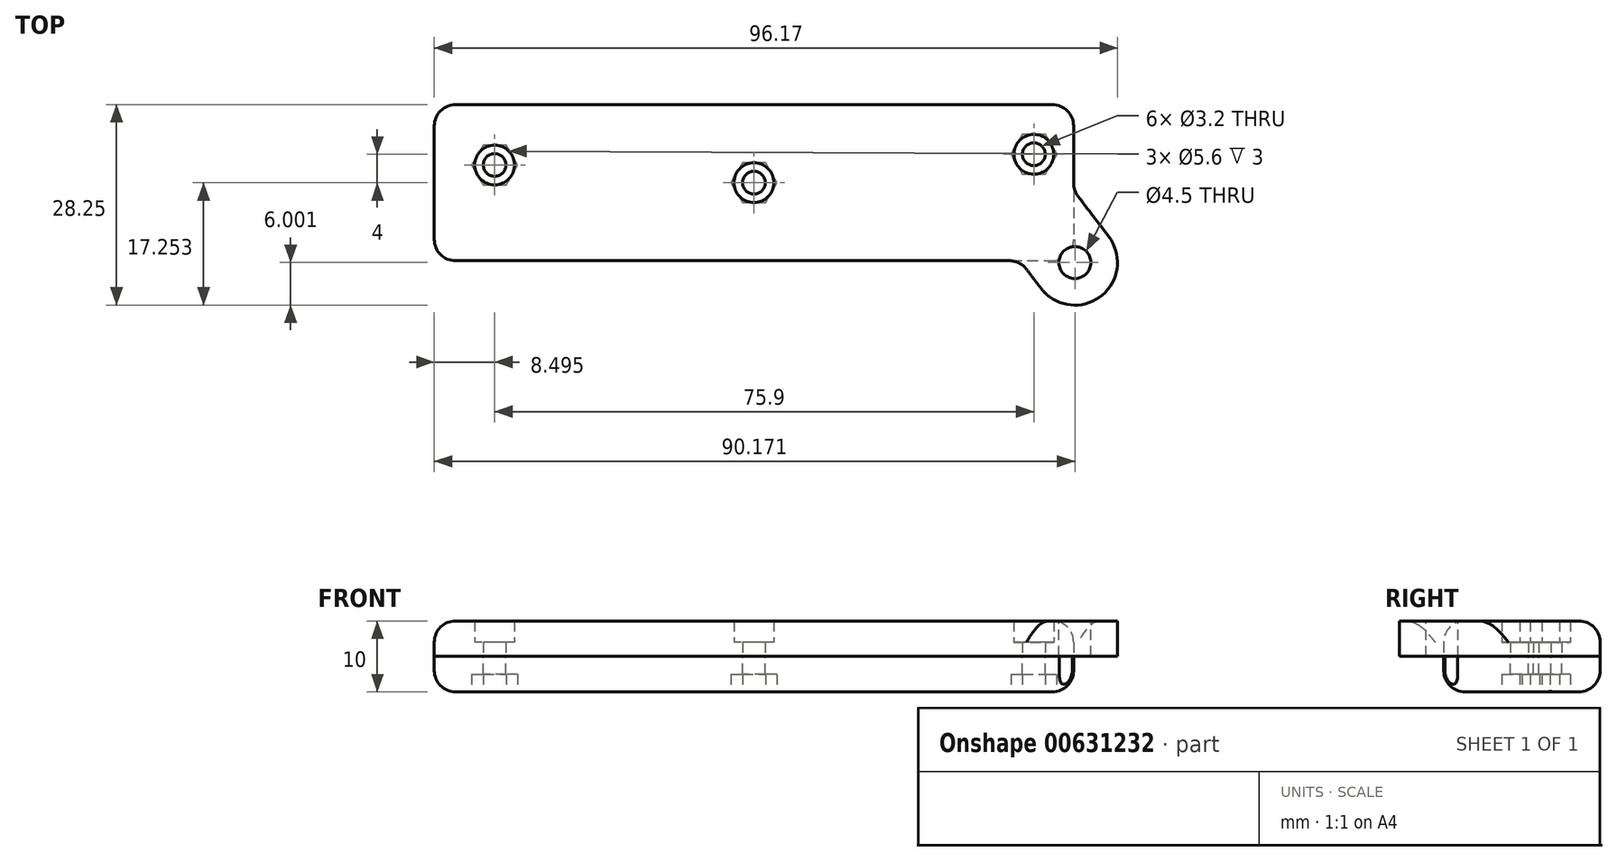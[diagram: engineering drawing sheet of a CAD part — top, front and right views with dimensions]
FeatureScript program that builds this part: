
annotation { "Feature Type Name" : "Feature", "Feature Type Description" : "" }
export const myFeature = defineFeature(function(context is Context, id is Id, definition is map)
    precondition{}
    {
        {
            var Q0;
            Q0=qCreatedBy(makeId("Top.planeOp"),FACE);
            var sketch = newSketch(context, id + "F0", { "sketchPlane" : qUnion([Q0])});
            skLineSegment(sketch, "E0.bottom", {"start": v(-43.13, 4.52) * mm, "end": v(46.87, 4.52) * mm});
            skLineSegment(sketch, "E0.top", {"start": v(-43.13, -17.48) * mm, "end": v(46.87, -17.48) * mm});
            skLineSegment(sketch, "E0.left", {"start": v(-43.13, 4.52) * mm, "end": v(-43.13, -17.48) * mm});
            skLineSegment(sketch, "E0.right", {"start": v(46.87, 4.52) * mm, "end": v(46.87, -17.48) * mm});
            skCircle(sketch, "E1", {"center": v(-34.63, -3.98) * mm, "radius": 1.6 * mm});
            skCircle(sketch, "E2", {"center": v(41.27, -2.48) * mm, "radius": 1.6 * mm});
            skCircle(sketch, "E3", {"center": v(1.87, -6.48) * mm, "radius": 1.6 * mm});
            skCircle(sketch, "E4", {"center": v(47.04, -17.73) * mm, "radius": 6 * mm});
            skLineSegment(sketch, "E5", {"start": v(42.26, -21.35) * mm, "end": v(39.32, -17.48) * mm});
            skLineSegment(sketch, "E6", {"start": v(42.26, -21.35) * mm, "end": v(51.82, -14.1) * mm, "construction": true});
            skLineSegment(sketch, "E7", {"start": v(51.82, -14.1) * mm, "end": v(46.87, -7.56) * mm});
            skSolve(sketch);
        }
        {
            var Q0;
            Q0=makeQuery(id+"F0.imprint","IMPRINT",FACE,{"disambiguationData":[TD([[makeQuery(id+"F0.imprint","IMPRINT",EDGE,{"derivedFrom":sQuery(id+"F0.wireOp",EDGE,"E0.bottom")}),-1.0]])]});
            var Q1;
            {var subQ0=sQuery(id+"F0.wireOp",EDGE,"E5");Q1=makeQuery(id+"F0.imprint","IMPRINT",FACE,{"disambiguationData":[TD([[makeQuery(id+"F0.imprint","IMPRINT",EDGE,{"derivedFrom":subQ0}),-1.0]])]});}
            var Q2;
            {var subQ0=sQuery(id+"F0.wireOp",EDGE,"E0.right");var subQ1=sQuery(id+"F0.wireOp",EDGE,"E0.top");var subQ2=makeQuery(id+"F0.imprint","INTERSECT",VERTEX,{"derivedFrom":[subQ1,subQ0]});Q2=makeQuery(id+"F0.imprint","IMPRINT",FACE,{"disambiguationData":[TD([[makeQuery(id+"F0.imprint","IMPRINT",EDGE,{"disambiguationData":[TD([[subQ2,1.0]])],"derivedFrom":subQ1}),1.0]])]});}
            var Q3;
            Q3=makeQuery(id+"F0.imprint","IMPRINT",FACE,{"disambiguationData":[TD([[makeQuery(id+"F0.imprint","IMPRINT",EDGE,{"derivedFrom":sQuery(id+"F0.wireOp",EDGE,"HLLScoW3-gvS7-jEic-zDn5-M5LXj1PQ8C7u")}),-1.0]])]});
            var Q4;
            {var subQ0=sQuery(id+"F0.wireOp",EDGE,"E7");Q4=makeQuery(id+"F0.imprint","IMPRINT",FACE,{"disambiguationData":[TD([[makeQuery(id+"F0.imprint","IMPRINT",EDGE,{"derivedFrom":subQ0}),1.0]])]});}
            var Q5;
            {var subQ2=sQuery(id+"F0.wireOp",EDGE,"E0.right");var subQ4=sQuery(id+"F0.wireOp",EDGE,"E0.top");var subQ5=makeQuery(id+"F0.imprint","INTERSECT",VERTEX,{"derivedFrom":[subQ4,subQ2]});Q5=makeQuery(id+"F0.imprint","IMPRINT",FACE,{"disambiguationData":[TD([[makeQuery(id+"F0.imprint","IMPRINT",EDGE,{"disambiguationData":[TD([[subQ5,1.0]])],"derivedFrom":subQ4}),-1.0]])]});}
            extrude(context, id + "F1", {"entities" : qUnion([Q0, Q1, Q2, Q3, Q4, Q5]), "depth" : 2 * mm, "offsetDistance" : 25 * mm});
        }
        {
            var Q0;
            Q0=makeQuery(id+"F1.opExtrude","CAP_FACE",FACE,{"disambiguationData":[OSD([sQuery(id+"F0.wireOp",EDGE,"E0.bottom"),sQuery(id+"F0.wireOp",EDGE,"E0.top"),sQuery(id+"F0.wireOp",EDGE,"E0.left"),sQuery(id+"F0.wireOp",EDGE,"E0.right"),sQuery(id+"F0.wireOp",EDGE,"E1"),sQuery(id+"F0.wireOp",EDGE,"E2"),sQuery(id+"F0.wireOp",EDGE,"E3")])],"isStart":false});
            var sketch = newSketch(context, id + "F2", { "sketchPlane" : qUnion([Q0])});
            skCircle(sketch, "E8.0", {"center": v(-34.63, -3.98) * mm, "radius": 2.8 * mm});
            skCircle(sketch, "E9.0", {"center": v(1.87, -6.48) * mm, "radius": 2.8 * mm});
            skCircle(sketch, "E10.0", {"center": v(41.27, -2.48) * mm, "radius": 2.8 * mm});
            skSolve(sketch);
        }
        {
            var Q0;
            Q0=makeQuery(id+"F2.imprint","IMPRINT",FACE,{"disambiguationData":[TD([[makeQuery(id+"F2.imprint","IMPRINT",EDGE,{"derivedFrom":sQuery(id+"F2.wireOp",EDGE,"E8.0")}),-1.0]])]});
            extrude(context, id + "F3", {"entities" : qUnion([Q0]), "operationType" : NewBodyOperationType.ADD, "depth" : 3 * mm, "offsetDistance" : 25 * mm});
        }
        {
            var Q0;
            Q0=makeQuery(id+"F3.opExtrude","CAP_EDGE",EDGE,{"disambiguationData":[OSD([sQuery(id+"F0.wireOp",EDGE,"E0.left")])],"isStart":false});
            var Q1;
            Q1=makeQuery(id+"F3.opExtrude","CAP_EDGE",EDGE,{"disambiguationData":[OSD([sQuery(id+"F0.wireOp",EDGE,"E0.bottom")])],"isStart":false});
            var Q2;
            Q2=makeQuery(id+"F3.opExtrude","CAP_EDGE",EDGE,{"disambiguationData":[OSD([sQuery(id+"F0.wireOp",EDGE,"E0.top")])],"isStart":false});
            var Q3;
            Q3=makeQuery(id+"F3.opExtrude","CAP_EDGE",EDGE,{"disambiguationData":[OSD([sQuery(id+"F0.wireOp",EDGE,"E0.right")])],"isStart":false});
            var Q4;
            {var subQ0=sQuery(id+"F0.wireOp",EDGE,"E0.right");var subQ1=sQuery(id+"F0.wireOp",EDGE,"E0.top");Q4=makeQuery(id+"F3.boolean.opBoolean","MERGE",EDGE,{"derivedFrom":[makeQuery(id+"F1.opExtrude","SWEPT_EDGE",EDGE,{"disambiguationData":[OSD([subQ1,subQ0])]}),makeQuery(id+"F3.opExtrude","SWEPT_EDGE",EDGE,{"disambiguationData":[OSD([subQ1,subQ0])]})]});}
            var Q5;
            {var subQ0=sQuery(id+"F0.wireOp",EDGE,"E0.right");var subQ1=sQuery(id+"F0.wireOp",EDGE,"E0.bottom");Q5=makeQuery(id+"F3.boolean.opBoolean","MERGE",EDGE,{"derivedFrom":[makeQuery(id+"F1.opExtrude","SWEPT_EDGE",EDGE,{"disambiguationData":[OSD([subQ1,subQ0])]}),makeQuery(id+"F3.opExtrude","SWEPT_EDGE",EDGE,{"disambiguationData":[OSD([subQ1,subQ0])]})]});}
            var Q6;
            {var subQ0=sQuery(id+"F0.wireOp",EDGE,"E0.left");var subQ1=sQuery(id+"F0.wireOp",EDGE,"E0.bottom");Q6=makeQuery(id+"F3.boolean.opBoolean","MERGE",EDGE,{"derivedFrom":[makeQuery(id+"F1.opExtrude","SWEPT_EDGE",EDGE,{"disambiguationData":[OSD([subQ1,subQ0])]}),makeQuery(id+"F3.opExtrude","SWEPT_EDGE",EDGE,{"disambiguationData":[OSD([subQ1,subQ0])]})]});}
            var Q7;
            {var subQ0=sQuery(id+"F0.wireOp",EDGE,"E0.left");var subQ1=sQuery(id+"F0.wireOp",EDGE,"E0.top");Q7=makeQuery(id+"F3.boolean.opBoolean","MERGE",EDGE,{"derivedFrom":[makeQuery(id+"F1.opExtrude","SWEPT_EDGE",EDGE,{"disambiguationData":[OSD([subQ1,subQ0])]}),makeQuery(id+"F3.opExtrude","SWEPT_EDGE",EDGE,{"disambiguationData":[OSD([subQ1,subQ0])]})]});}
            fillet(context, id + "F4", {"entities" : qUnion([Q0, Q1, Q2, Q3, Q4, Q5, Q6, Q7]), "radius" : 3 * mm, "tangentPropagation" : true, "allowEdgeOverflow" : false});
        }
        {
            var Q0;
            Q0=makeQuery(id+"F3.opExtrude","CAP_FACE",FACE,{"disambiguationData":[OSD([sQuery(id+"F0.wireOp",EDGE,"E0.bottom"),sQuery(id+"F0.wireOp",EDGE,"E0.top"),sQuery(id+"F0.wireOp",EDGE,"E0.left"),sQuery(id+"F0.wireOp",EDGE,"E0.right"),sQuery(id+"F0.wireOp",EDGE,"E4"),sQuery(id+"F0.wireOp",EDGE,"E5"),sQuery(id+"F0.wireOp",EDGE,"E7"),sQuery(id+"F2.wireOp",EDGE,"E8.0"),sQuery(id+"F2.wireOp",EDGE,"E9.0"),sQuery(id+"F2.wireOp",EDGE,"E10.0")])],"isStart":false});
            var sketch = newSketch(context, id + "F5", { "sketchPlane" : qUnion([Q0])});
            skCircle(sketch, "E11", {"center": v(47.04, -17.73) * mm, "radius": 2.25 * mm});
            skSolve(sketch);
        }
        {
            var Q0;
            Q0 = qSketchRegion(id + "F5", true);
            extrude(context, id + "F6", {"entities" : qUnion([Q0]), "operationType" : NewBodyOperationType.REMOVE, "endBound" : BoundingType.UP_TO_NEXT, "oppositeDirection" : true, "depth" : 25 * mm, "offsetDistance" : 25 * mm});
        }
        {
            var Q0;
            {var subQ7=sQuery(id+"F0.wireOp",EDGE,"E0.bottom");Q0=makeQuery(id+"F0.imprint","IMPRINT",FACE,{"disambiguationData":[TD([[makeQuery(id+"F0.imprint","IMPRINT",EDGE,{"derivedFrom":subQ7}),-1.0]])]});}
            var Q1;
            {var subQ0=sQuery(id+"F0.wireOp",EDGE,"E0.right");var subQ1=sQuery(id+"F0.wireOp",EDGE,"E0.top");var subQ2=makeQuery(id+"F0.imprint","INTERSECT",VERTEX,{"derivedFrom":[subQ1,subQ0]});Q1=makeQuery(id+"F0.imprint","IMPRINT",FACE,{"disambiguationData":[TD([[makeQuery(id+"F0.imprint","IMPRINT",EDGE,{"disambiguationData":[TD([[subQ2,1.0]])],"derivedFrom":subQ1}),1.0]])]});}
            extrude(context, id + "F7", {"entities" : qUnion([Q0, Q1]), "oppositeDirection" : true, "depth" : 5 * mm, "offsetDistance" : 25 * mm});
        }
        {
            var Q0;
            Q0=makeQuery(id+"F7.opExtrude","SWEPT_EDGE",EDGE,{"disambiguationData":[OSD([sQuery(id+"F0.wireOp",EDGE,"E0.bottom"),sQuery(id+"F0.wireOp",EDGE,"E0.right")])]});
            var Q1;
            Q1=makeQuery(id+"F7.opExtrude","SWEPT_EDGE",EDGE,{"disambiguationData":[OSD([sQuery(id+"F0.wireOp",EDGE,"E0.top"),sQuery(id+"F0.wireOp",EDGE,"E0.right")])]});
            var Q2;
            Q2=makeQuery(id+"F7.opExtrude","CAP_EDGE",EDGE,{"disambiguationData":[OSD([sQuery(id+"F0.wireOp",EDGE,"E0.right")])],"isStart":false});
            var Q3;
            Q3=makeQuery(id+"F7.opExtrude","CAP_EDGE",EDGE,{"disambiguationData":[OSD([sQuery(id+"F0.wireOp",EDGE,"E0.top")])],"isStart":false});
            var Q4;
            Q4=makeQuery(id+"F7.opExtrude","CAP_EDGE",EDGE,{"disambiguationData":[OSD([sQuery(id+"F0.wireOp",EDGE,"E0.bottom")])],"isStart":false});
            var Q5;
            Q5=makeQuery(id+"F7.opExtrude","CAP_EDGE",EDGE,{"disambiguationData":[OSD([sQuery(id+"F0.wireOp",EDGE,"E0.left")])],"isStart":false});
            var Q6;
            Q6=makeQuery(id+"F7.opExtrude","SWEPT_EDGE",EDGE,{"disambiguationData":[OSD([sQuery(id+"F0.wireOp",EDGE,"E0.bottom"),sQuery(id+"F0.wireOp",EDGE,"E0.left")])]});
            var Q7;
            Q7=makeQuery(id+"F7.opExtrude","SWEPT_EDGE",EDGE,{"disambiguationData":[OSD([sQuery(id+"F0.wireOp",EDGE,"E0.top"),sQuery(id+"F0.wireOp",EDGE,"E0.left")])]});
            fillet(context, id + "F8", {"entities" : qUnion([Q0, Q1, Q2, Q3, Q4, Q5, Q6, Q7]), "radius" : 3 * mm, "tangentPropagation" : true, "allowEdgeOverflow" : false});
        }
        {
            var Q0;
            Q0 = qSketchRegion(id + "F5", true);
            extrude(context, id + "F9", {"entities" : qUnion([Q0]), "operationType" : NewBodyOperationType.REMOVE, "oppositeDirection" : true, "depth" : 25 * mm, "offsetDistance" : 25 * mm});
        }
        {
            var Q0;
            Q0=makeQuery(id+"F7.opExtrude","CAP_FACE",FACE,{"disambiguationData":[OSD([sQuery(id+"F0.wireOp",EDGE,"E0.bottom"),sQuery(id+"F0.wireOp",EDGE,"E0.top"),sQuery(id+"F0.wireOp",EDGE,"E0.left"),sQuery(id+"F0.wireOp",EDGE,"E0.right"),sQuery(id+"F0.wireOp",EDGE,"E1"),sQuery(id+"F0.wireOp",EDGE,"E2"),sQuery(id+"F0.wireOp",EDGE,"E3")])],"isStart":false});
            var sketch = newSketch(context, id + "F10", { "sketchPlane" : qUnion([Q0])});
            skCircle(sketch, "E12.cCircle", {"center": v(-34.63, 3.98) * mm, "radius": 2.8 * mm, "construction": true});
            skLineSegment(sketch, "E12.0", {"start": v(-33.02, 1.18) * mm, "end": v(-36.25, 1.18) * mm});
            skLineSegment(sketch, "E12.1", {"start": v(-36.25, 1.18) * mm, "end": v(-37.87, 3.98) * mm});
            skLineSegment(sketch, "E12.2", {"start": v(-37.87, 3.98) * mm, "end": v(-36.25, 6.78) * mm});
            skLineSegment(sketch, "E12.3", {"start": v(-36.25, 6.78) * mm, "end": v(-33.02, 6.78) * mm});
            skLineSegment(sketch, "E12.4", {"start": v(-33.02, 6.78) * mm, "end": v(-31.4, 3.98) * mm});
            skLineSegment(sketch, "E12.5", {"start": v(-31.4, 3.98) * mm, "end": v(-33.02, 1.18) * mm});
            skPoint(sketch, "E12.0.midPoint", {"position": v(-34.63, 1.18) * mm});
            skCircle(sketch, "E13.cCircle", {"center": v(1.87, 6.48) * mm, "radius": 2.8 * mm, "construction": true});
            skLineSegment(sketch, "E13.0", {"start": v(3.48, 3.68) * mm, "end": v(0.25, 3.68) * mm});
            skLineSegment(sketch, "E13.1", {"start": v(0.25, 3.68) * mm, "end": v(-1.37, 6.48) * mm});
            skLineSegment(sketch, "E13.2", {"start": v(-1.37, 6.48) * mm, "end": v(0.25, 9.28) * mm});
            skLineSegment(sketch, "E13.3", {"start": v(0.25, 9.28) * mm, "end": v(3.48, 9.28) * mm});
            skLineSegment(sketch, "E13.4", {"start": v(3.48, 9.28) * mm, "end": v(5.1, 6.48) * mm});
            skLineSegment(sketch, "E13.5", {"start": v(5.1, 6.48) * mm, "end": v(3.48, 3.68) * mm});
            skPoint(sketch, "E13.0.midPoint", {"position": v(1.87, 3.68) * mm});
            skCircle(sketch, "E14.cCircle", {"center": v(41.27, 2.48) * mm, "radius": 2.8 * mm, "construction": true});
            skLineSegment(sketch, "E14.0", {"start": v(39.65, 5.28) * mm, "end": v(42.88, 5.28) * mm});
            skLineSegment(sketch, "E14.1", {"start": v(42.88, 5.28) * mm, "end": v(44.5, 2.48) * mm});
            skLineSegment(sketch, "E14.2", {"start": v(44.5, 2.48) * mm, "end": v(42.88, -0.32) * mm});
            skLineSegment(sketch, "E14.3", {"start": v(42.88, -0.32) * mm, "end": v(39.65, -0.32) * mm});
            skLineSegment(sketch, "E14.4", {"start": v(39.65, -0.32) * mm, "end": v(38.03, 2.48) * mm});
            skLineSegment(sketch, "E14.5", {"start": v(38.03, 2.48) * mm, "end": v(39.65, 5.28) * mm});
            skPoint(sketch, "E14.0.midPoint", {"position": v(41.27, 5.28) * mm});
            skSolve(sketch);
        }
        {
            var Q0;
            Q0 = qSketchRegion(id + "F10", true);
            extrude(context, id + "F11", {"entities" : qUnion([Q0]), "operationType" : NewBodyOperationType.REMOVE, "oppositeDirection" : true, "depth" : 2.5 * mm, "offsetDistance" : 25 * mm});
        }
    });
